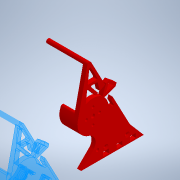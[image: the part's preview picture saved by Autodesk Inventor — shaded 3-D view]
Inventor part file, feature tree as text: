
AUTODESK INVENTOR PART (.ipt)
format: ipt  version: 2020 (Build 240168000, 168)  size: 617,472 bytes
history: native  units: mm
features: extrude x14, sketch x12, fillet x4, other x3, chamfer x1, projected_geometry x1
ambient origin geometry x8: Origin, YZ Plane, XZ Plane, XY Plane, X Axis, Y Axis, Z Axis, Center Point
bodies: Solid1 (feature_tree)
feature tree (35):
  other  "WeaponMountBasePlateV1.ipt"
  extrude  "Extrusion1"  Depth=10.0mm
  extrude  "Extrusion2"  Depth=0.5mm
  extrude  "Extrusion3"  Depth=4.5mm
  extrude  "Extrusion4"  Depth=16.0mm
  fillet  "Fillet1"  Radius=3.1mm
  extrude  "Extrusion5"  Depth=19.0mm
  fillet  "Fillet3"  Radius=3.1mm
  extrude  "Extrusion6"  TaperAngle=0.0deg  [1 undecoded]
  extrude  "Extrusion7"  TaperAngle=0.0deg  [1 undecoded]
  extrude  "Extrusion8"  Depth=17.0mm TaperAngle=0.0deg
  extrude  "Extrusion9"  Depth=2.5mm
  extrude  "Extrusion10"  Depth=7.0mm TaperAngle=0.0deg
  fillet  "Fillet4"  Radius=1.0mm
  extrude  "Extrusion11"  Depth=4.0mm
  chamfer  "Chamfer1"  Distance=9.0mm
  extrude  "Extrusion12"  Depth=2.0mm
  extrude  "Extrusion15"  Depth=2.0mm
  extrude  "Extrusion16"  Depth=2.0mm
  fillet  "Fillet6"  Radius=61.487mm
  other  "Solid1::WeaponMountBasePlateV1.ipt"
  other  "TaggingFeature1"
  sketch  "Sketch2"  dims[d0=10.0mm d2=27.8mm]
  sketch  "Sketch3"  dims[d3=5.0mm d4=0.5mm]
  sketch  "Sketch4"  dims[d5=17.0mm d6=0.0mm d7=4.5mm]
  sketch  "Sketch6"  dims[d8=17.0mm d9=0.0mm d10=16.0mm d11=3.1mm]
  sketch  "Sketch8"  dims[d12=3.1mm d13=19.0mm d14=3.1mm]
  sketch  "Sketch9"  dims[d15=3.1mm d16=0.0mm d17=0.0mm]
  sketch  "Sketch10"  dims[d18=180.0deg d19=0.0mm]
  projected_geometry  "Projected Loop1"
  sketch  "Sketch11"  dims[d20=4.363323mm d21=17.0mm d22=0.0mm]
  sketch  "Sketch12"  dims[d23=10.0mm d25=2.5mm]
  sketch  "Sketch13"  dims[d27=12.0mm d28=7.0mm d29=0.0mm d30=1.0mm]
  sketch  "Sketch14"  dims[d31=13.0mm d32=4.0mm]
  sketch  "Sketch15"  dims[d33=10.0mm d34=9.0mm d35=0.0mm d36=2.0mm d37=2.0mm d39=2.0mm d40=61.487mm d41=0.0mm d43=3.490659mm d45=45.0mm d46=0.0mm d47=2.1mm d48=6.0mm d49=0.0mm d50=6.1mm d51=6.1mm d52=6.0mm d53=-7.853982mm d54=1.0mm d55=8.5mm d56=3.0mm d57=0.0mm d58=1.0mm d59=2.0mm d60=45.0deg d61=10.0mm d62=0.0mm d81=0.0mm d82=0.0mm d83=10.0mm d84=0.0mm d87=4.0mm d88=3.0mm d89=3.0mm d90=1.5mm d91=1.5mm d92=1.5mm d93=1.5mm d94=2.0mm]
note: 2 required parameter values undecoded (feature->parameter linkage not recoverable at this tier; creation-order binding heuristic only, values carry confidence <= 0.55)
